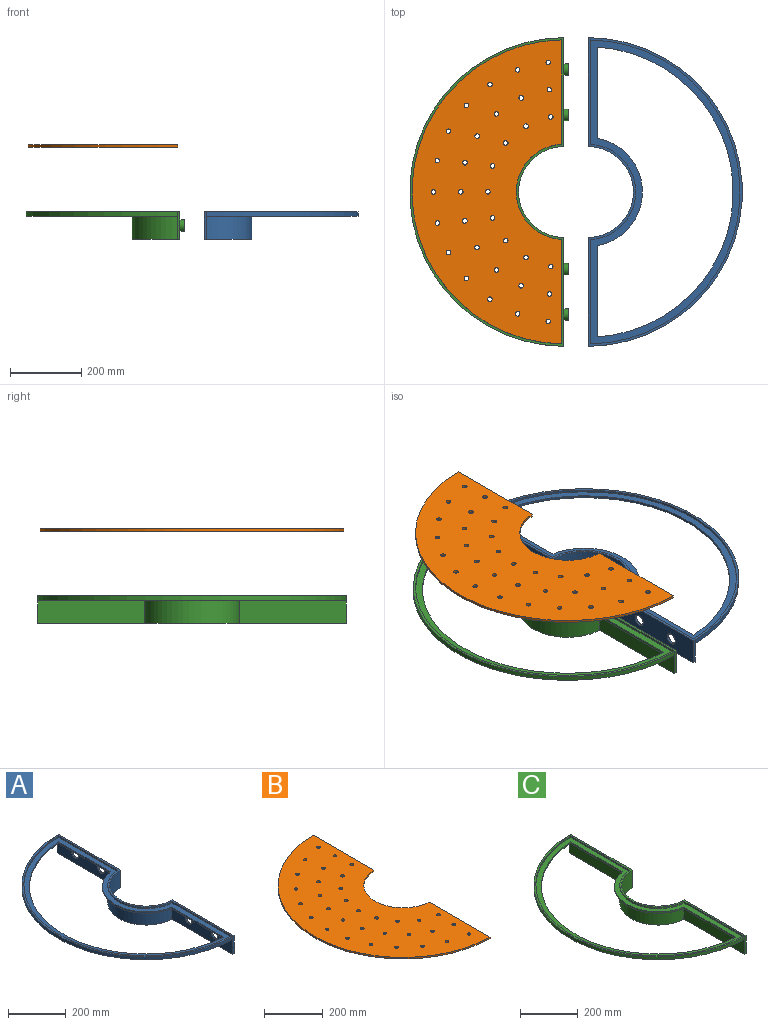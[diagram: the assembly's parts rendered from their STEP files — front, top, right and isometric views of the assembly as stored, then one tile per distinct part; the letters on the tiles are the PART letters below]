
ASSEMBLY  parts=3 mates=2
PART A: 25 faces, bbox 431.8x863.6x76.2 mm
  f0: cylinder r=431.8mm len=863.51mm, axis (0,0,-1), area 17066.8mm2, adj f1,f2,f15,f18
  f1: plane 863.51x425.45mm, normal (0,0,-1), area 51128.4mm2, adj f0,f3,f4,f5,f6,f15,f18,f20
  f2: plane 863.6x431.8mm, normal (0,0,1), area 14857.9mm2, adj f0,f7,f8,f9,f10,f11,f12,f13
  f3: plane 255.34x6.35mm, normal (-1,0,0), area 1621.4mm2, adj f1,f4,f6,f14
  f4: cylinder r=152.4mm len=300.54mm, axis (0,0,1), area 2716.2mm2, adj f1,f3,f5,f14
  f5: plane 255.34x6.35mm, normal (-1,0,0), area 1621.4mm2, adj f1,f4,f6,f14
  f6: cylinder r=406.4mm len=811.21mm, axis (0,0,1), area 7784.5mm2, adj f1,f3,f5,f14
  f7: cylinder r=127mm len=254mm, axis (0,0,-1), area 30402.4mm2, adj f2,f8,f9,f17
  f8: plane 304.8x76.2mm, normal (1,0,0), area 21642.3mm2, adj f2,f7,f16,f17,f23,f24
  f9: plane 304.8x76.2mm, normal (1,0,0), area 21642.3mm2, adj f2,f7,f17,f19,f21,f22
  f10: plane 292.2x6.35mm, normal (-1,0,0), area 1855.5mm2, adj f2,f11,f13,f14
  f11: cylinder r=133.35mm len=266.4mm, axis (0,0,1), area 2579.5mm2, adj f2,f10,f12,f14
  f12: plane 292.2x6.35mm, normal (-1,0,0), area 1855.5mm2, adj f2,f11,f13,f14
  f13: cylinder r=425.45mm len=850.81mm, axis (0,0,1), area 8406.7mm2, adj f2,f10,f12,f14
  f14: plane 850.81x419.1mm, normal (0,0,1), area 42658.3mm2, adj f3,f4,f5,f6,f10,f11,f12,f13
  f15: plane 298.6x76.2mm, normal (-1,0,0), area 17378.3mm2, adj f0,f1,f2,f16,f17,f20,f23,f24
  f16: plane 76.2x6.35mm, normal (0,-1,0), area 483.9mm2, adj f2,f8,f15,f17
  f17: plane 863.6x133.35mm, normal (0,0,-1), area 6387.8mm2, adj f7,f8,f9,f15,f16,f18,f19,f20
  f18: plane 298.6x76.2mm, normal (-1,0,0), area 17378.3mm2, adj f0,f1,f2,f17,f19,f20,f21,f22
  f19: plane 76.2x6.35mm, normal (0,1,0), area 483.9mm2, adj f2,f9,f17,f18
  f20: cylinder r=133.35mm len=266.4mm, axis (0,0,1), area 25795.4mm2, adj f1,f15,f17,f18
  f21: cylinder r=15.88mm len=31.75mm, axis (1,0,0), area 633.4mm2, adj f9,f18
  f22: cylinder r=15.88mm len=31.75mm, axis (1,0,0), area 633.4mm2, adj f9,f18
  f23: cylinder r=15.88mm len=31.75mm, axis (1,0,0), area 633.4mm2, adj f8,f15
  f24: cylinder r=15.88mm len=31.75mm, axis (1,0,0), area 633.4mm2, adj f8,f15
PART B: 39 faces, bbox 419.1x850.8x6.4 mm
  f0: cylinder r=133.35mm len=266.4mm, axis (0,0,-1), area 2579.5mm2, adj f2,f3,f37,f38
  f1: cylinder r=425.45mm len=850.81mm, axis (0,0,-1), area 8406.7mm2, adj f2,f3,f37,f38
  f2: plane 850.81x419.1mm, normal (0,0,1), area 248503.5mm2, adj f0,f1,f4,f5,f6,f7,f8,f9
  f3: plane 850.81x419.1mm, normal (0,0,-1), area 248503.5mm2, adj f0,f1,f4,f5,f6,f7,f8,f9
  f4: cylinder r=6.35mm len=12.7mm, axis (0,0,1), area 253.4mm2, adj f2,f3
  f5: cylinder r=6.35mm len=12.7mm, axis (0,0,1), area 253.4mm2, adj f2,f3
  f6: cylinder r=6.35mm len=12.7mm, axis (0,0,1), area 253.4mm2, adj f2,f3
  f7: cylinder r=6.35mm len=12.7mm, axis (0,0,1), area 253.4mm2, adj f2,f3
  f8: cylinder r=6.35mm len=12.7mm, axis (0,0,1), area 253.4mm2, adj f2,f3
  f9: cylinder r=6.35mm len=12.7mm, axis (0,0,1), area 253.4mm2, adj f2,f3
  f10: cylinder r=6.35mm len=12.7mm, axis (0,0,1), area 253.4mm2, adj f2,f3
  f11: cylinder r=6.35mm len=12.7mm, axis (0,0,1), area 253.4mm2, adj f2,f3
  f12: cylinder r=6.35mm len=12.7mm, axis (0,0,1), area 253.4mm2, adj f2,f3
  f13: cylinder r=6.35mm len=12.7mm, axis (0,0,1), area 253.4mm2, adj f2,f3
  f14: cylinder r=6.35mm len=12.7mm, axis (0,0,1), area 253.4mm2, adj f2,f3
  f15: cylinder r=6.35mm len=12.7mm, axis (0,0,1), area 253.4mm2, adj f2,f3
  f16: cylinder r=6.35mm len=12.7mm, axis (0,0,1), area 253.4mm2, adj f2,f3
  f17: cylinder r=6.35mm len=12.7mm, axis (0,0,1), area 253.4mm2, adj f2,f3
  f18: cylinder r=6.35mm len=12.7mm, axis (0,0,1), area 253.4mm2, adj f2,f3
  f19: cylinder r=6.35mm len=12.7mm, axis (0,0,1), area 253.4mm2, adj f2,f3
  f20: cylinder r=6.35mm len=12.7mm, axis (0,0,1), area 253.4mm2, adj f2,f3
  f21: cylinder r=6.35mm len=12.7mm, axis (0,0,1), area 253.4mm2, adj f2,f3
  f22: cylinder r=6.35mm len=12.7mm, axis (0,0,1), area 253.4mm2, adj f2,f3
  f23: cylinder r=6.35mm len=12.7mm, axis (0,0,1), area 253.4mm2, adj f2,f3
  f24: cylinder r=6.35mm len=12.7mm, axis (0,0,1), area 253.4mm2, adj f2,f3
  f25: cylinder r=6.35mm len=12.7mm, axis (0,0,1), area 253.4mm2, adj f2,f3
  f26: cylinder r=6.35mm len=12.7mm, axis (0,0,1), area 253.4mm2, adj f2,f3
  f27: cylinder r=6.35mm len=12.7mm, axis (0,0,1), area 253.4mm2, adj f2,f3
  f28: cylinder r=6.35mm len=12.7mm, axis (0,0,1), area 253.4mm2, adj f2,f3
  f29: cylinder r=6.35mm len=12.7mm, axis (0,0,1), area 253.4mm2, adj f2,f3
  f30: cylinder r=6.35mm len=12.7mm, axis (0,0,1), area 253.4mm2, adj f2,f3
  f31: cylinder r=6.35mm len=12.7mm, axis (0,0,1), area 253.4mm2, adj f2,f3
  f32: cylinder r=6.35mm len=12.7mm, axis (0,0,1), area 253.4mm2, adj f2,f3
  f33: cylinder r=6.35mm len=12.7mm, axis (0,0,1), area 253.4mm2, adj f2,f3
  f34: cylinder r=6.35mm len=12.7mm, axis (0,0,1), area 253.4mm2, adj f2,f3
  f35: cylinder r=6.35mm len=12.7mm, axis (0,0,1), area 253.4mm2, adj f2,f3
  f36: cylinder r=6.35mm len=12.7mm, axis (0,0,1), area 253.4mm2, adj f2,f3
  f37: plane 292.2x6.35mm, normal (1,0,0), area 1855.5mm2, adj f0,f1,f2,f3
  f38: plane 292.2x6.35mm, normal (1,0,0), area 1855.5mm2, adj f0,f1,f2,f3
PART C: 29 faces, bbox 444.5x863.6x76.2 mm
  f0: cylinder r=431.8mm len=863.51mm, axis (0,0,-1), area 17066.8mm2, adj f1,f2,f15,f18
  f1: plane 863.51x425.45mm, normal (0,0,-1), area 51128.4mm2, adj f0,f3,f4,f5,f6,f15,f18,f20
  f2: plane 863.6x431.8mm, normal (0,0,1), area 14857.9mm2, adj f0,f7,f8,f9,f10,f11,f12,f13
  f3: plane 255.34x6.35mm, normal (-1,0,0), area 1621.4mm2, adj f1,f4,f6,f14
  f4: cylinder r=152.4mm len=300.54mm, axis (0,0,1), area 2716.2mm2, adj f1,f3,f5,f14
  f5: plane 255.34x6.35mm, normal (-1,0,0), area 1621.4mm2, adj f1,f4,f6,f14
  f6: cylinder r=406.4mm len=811.21mm, axis (0,0,1), area 7784.5mm2, adj f1,f3,f5,f14
  f7: cylinder r=127mm len=254mm, axis (0,0,-1), area 30402.4mm2, adj f2,f8,f9,f17
  f8: plane 304.8x76.2mm, normal (1,0,0), area 21642.3mm2, adj f2,f7,f16,f17,f21,f23
  f9: plane 304.8x76.2mm, normal (1,0,0), area 21642.3mm2, adj f2,f7,f17,f19,f25,f27
  f10: plane 292.2x6.35mm, normal (-1,0,0), area 1855.5mm2, adj f2,f11,f13,f14
  f11: cylinder r=133.35mm len=266.4mm, axis (0,0,1), area 2579.5mm2, adj f2,f10,f12,f14
  f12: plane 292.2x6.35mm, normal (-1,0,0), area 1855.5mm2, adj f2,f11,f13,f14
  f13: cylinder r=425.45mm len=850.81mm, axis (0,0,1), area 8406.7mm2, adj f2,f10,f12,f14
  f14: plane 850.81x419.1mm, normal (0,0,1), area 42658.3mm2, adj f3,f4,f5,f6,f10,f11,f12,f13
  f15: plane 298.6x76.2mm, normal (-1,0,0), area 18961.8mm2, adj f0,f1,f2,f16,f17,f20
  f16: plane 76.2x6.35mm, normal (0,-1,0), area 483.9mm2, adj f2,f8,f15,f17
  f17: plane 863.6x133.35mm, normal (0,0,-1), area 6387.8mm2, adj f7,f8,f9,f15,f16,f18,f19,f20
  f18: plane 298.6x76.2mm, normal (-1,0,0), area 18961.8mm2, adj f0,f1,f2,f17,f19,f20
  f19: plane 76.2x6.35mm, normal (0,1,0), area 483.9mm2, adj f2,f9,f17,f18
  f20: cylinder r=133.35mm len=266.4mm, axis (0,0,1), area 25795.4mm2, adj f1,f15,f17,f18
  f21: cylinder r=15.88mm len=31.75mm, axis (-1,0,0), area 1266.8mm2, adj f8,f22
  f22: plane 31.75x31.75mm, normal (1,0,0), area 791.7mm2, adj f21
  f23: cylinder r=15.88mm len=31.75mm, axis (-1,0,0), area 1266.8mm2, adj f8,f24
  f24: plane 31.75x31.75mm, normal (1,0,0), area 791.7mm2, adj f23
  f25: cylinder r=15.88mm len=31.75mm, axis (-1,0,0), area 1266.8mm2, adj f9,f26
  f26: plane 31.75x31.75mm, normal (1,0,0), area 791.7mm2, adj f25
  f27: cylinder r=15.88mm len=31.75mm, axis (-1,0,0), area 1266.8mm2, adj f9,f28
  f28: plane 31.75x31.75mm, normal (1,0,0), area 791.7mm2, adj f27
PLACE A rot(axis=(0,0,1),180deg) t=(72.69,-65.75,-32.8)mm
PLACE B t=(5.4,-65.75,161.37)mm
PLACE C t=(5.4,-65.75,-32.8)mm fixed
MATE slider B.f0 <-> C.f0  axis (0,0,-1) through (5.4,-65.75,161.37)mm
MATE slider C.f27 <-> A.f24  axis (1,0,0) through (5.4,150.15,-58.2)mm
